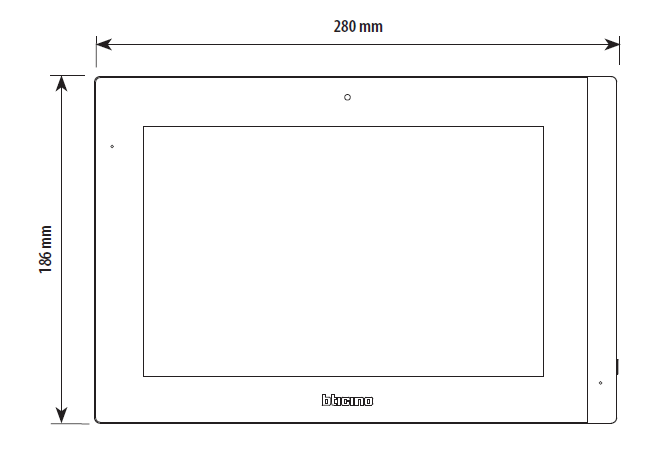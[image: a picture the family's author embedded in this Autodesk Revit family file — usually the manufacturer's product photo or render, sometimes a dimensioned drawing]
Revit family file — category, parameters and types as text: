
# Revit family: Legrand-Hotel_UX_ONE-Thermostat-EN
name_source: partatom
category: Equipement électrique
units: mm (PartAtom-declared; Revit-internal decimal feet)

## family parameters
Configuration du panneau = Deux colonnes, circuits au sein
Cote de connecteur circulaire = Utiliser le diamètre
Couper avec des vides une fois chargée = Non
Hôte = Face
Partagée = Non
Point de calcul de pièce = Non
Type d'élément = Tableau de raccordement

## types (8) — shared parameters
Built-in depth = 50 mm  [stored 0.164042 ft]
Configurator website = https://uxforhotels.legrand.com
Do not disturb function = Non
Elévation par défaut = 1500 mm  [stored 4.92126 ft]
Fabricant = LEGRAND
General Conditions of Use = https://export.legrand.com
Height = 93 mm  [stored 0.305118 ft]
IK = 04
IP = 20
Manual setpoint adjustment = Oui
Material = Plastic
Parallel operation possible = Oui
Radio bus system = Oui
Touchscreen = Oui
Width = 129 mm  [stored 0.423228 ft]
With display = Oui

## per-type parameters (varying)
| type | Color | Depth | Hauteur pictogrammes | Hauteur vide | Installation method | Matériau plaque | Matériau écran | Plaque apparente | Plaque encastrée | Product designation | Reference | Tension |
| Black 230V Recessed | Black | 52 mm | 0 mm  [stored 0 ft] | -40 mm  [stored -0.131234 ft] | Flush-mounting | LEGRAND_BLACK_PLASTIC | LEGRAND_BLACK_SCREEN | Non | Oui | FLUSH MOUNTING HOTEL THERMOSTAT BLACK  230V | LG-048900 | 230 V AC |
| Black 230V Surface | Black | 28 mm  [stored 0.0918635 ft] | 16 mm | 0 mm  [stored 0 ft] | surface | LEGRAND_BLACK_PLASTIC | LEGRAND_BLACK_SCREEN | Oui | Non | SURFACE HOTEL THERMOSTAT BLACK 230V | LG-048901 | 230 V AC |
| White 230V Recessed | White | 52 mm | 0 mm  [stored 0 ft] | -40 mm  [stored -0.131234 ft] | Flush-mounting | LEGRAND_WHITE_PLASTIC | LEGRAND_WHITE_SCREEN | Non | Oui | FLUSH MOUNTING HOTEL THERMOSTAT WHITE 230V | LG-048902 | 230 V AC |
| White 230V Surface | White | 28 mm  [stored 0.0918635 ft] | 16 mm | 0 mm  [stored 0 ft] | surface | LEGRAND_WHITE_PLASTIC | LEGRAND_WHITE_SCREEN | Oui | Non | SURFACE HOTEL THERMOSTAT WHITE  230V | LG-048903 | 230 V AC |
| Black 24V Recessed | Black | 52 mm | 0 mm  [stored 0 ft] | -40 mm  [stored -0.131234 ft] | Flush-mounting | LEGRAND_BLACK_PLASTIC | LEGRAND_BLACK_SCREEN | Non | Oui | FLUSH MOUNTING HOTEL THERMOSTAT BLACK 24V | LG-048904 | 24 V |
| Black 24V Surface | Black | 28 mm  [stored 0.0918635 ft] | 16 mm | 0 mm  [stored 0 ft] | surface | LEGRAND_BLACK_PLASTIC | LEGRAND_BLACK_SCREEN | Oui | Non | SURFACE HOTEL THERMOSTAT BLACK 24V | LG-048905 | 24 V |
| White 24V Recessed | White | 52 mm | 0 mm  [stored 0 ft] | -40 mm  [stored -0.131234 ft] | Flush-mounting | LEGRAND_WHITE_PLASTIC | LEGRAND_WHITE_SCREEN | Non | Oui | FLUSH MOUNTING HOTEL THERMOSTAT WHITE  24V | LG-048906 | 24 V |
| White 24V Surface | White | 28 mm  [stored 0.0918635 ft] | 16 mm | 0 mm  [stored 0 ft] | surface | LEGRAND_WHITE_PLASTIC | LEGRAND_WHITE_SCREEN | Oui | Non | SURFACE HOTEL THERMOSTAT WHITE 24V | LG-048907 | 24 V |

note: [stored X ft] marks values corroborated as IEEE doubles in the binary element streams (Revit-internal decimal feet)
